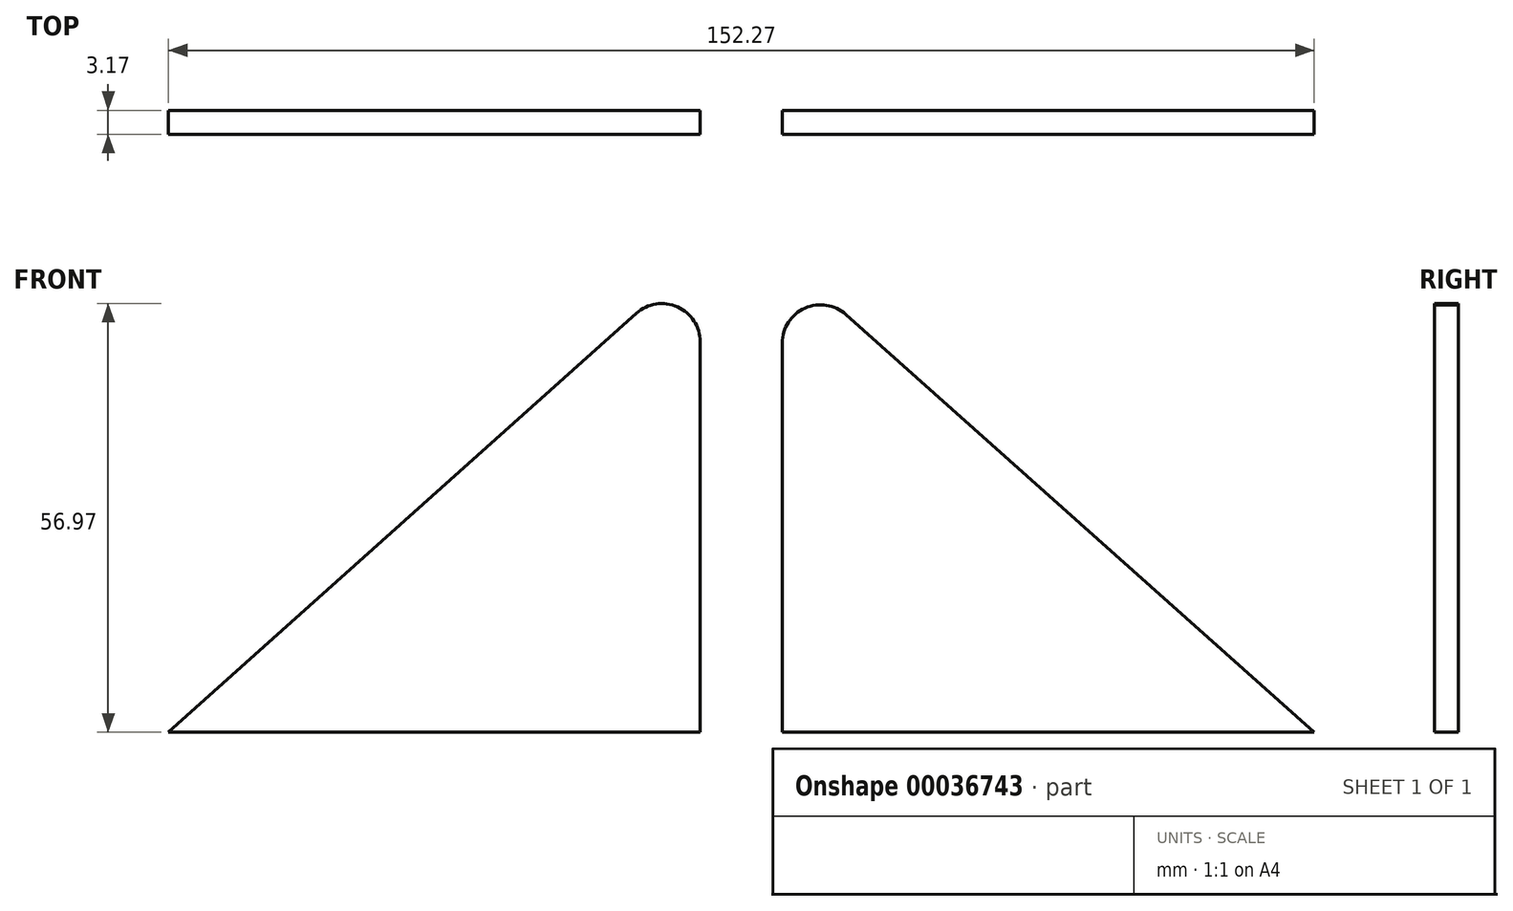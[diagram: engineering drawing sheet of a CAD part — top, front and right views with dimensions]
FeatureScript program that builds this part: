
annotation { "Feature Type Name" : "Feature", "Feature Type Description" : "" }
export const myFeature = defineFeature(function(context is Context, id is Id, definition is map)
    precondition{}
    {
        {
            var Q0;
            Q0=qCreatedBy(makeId("Front.planeOp"),FACE);
            var sketch = newSketch(context, id + "F0", { "sketchPlane" : qUnion([Q0])});
            skLineSegment(sketch, "E0", {"start": v(0, 63.5) * mm, "end": v(0, 0) * mm, "construction": true});
            skLineSegment(sketch, "E1", {"start": v(-5.58, 63.26) * mm, "end": v(-5.58, 0) * mm});
            skLineSegment(sketch, "E2", {"start": v(-5.58, 0) * mm, "end": v(-76.23, 0) * mm});
            skLineSegment(sketch, "E3", {"start": v(-76.23, 0) * mm, "end": v(-5.58, 63.26) * mm});
            skLineSegment(sketch, "E4", {"start": v(5.35, 63.06) * mm, "end": v(5.35, 0) * mm});
            skLineSegment(sketch, "E5", {"start": v(5.35, 0) * mm, "end": v(76.04, 0) * mm});
            skLineSegment(sketch, "E6", {"start": v(76.04, 0) * mm, "end": v(5.35, 63.06) * mm});
            skSolve(sketch);
        }
        {
            var Q0;
            Q0=makeQuery(id+"F0.imprint","IMPRINT",FACE,{"disambiguationData":[TD([[makeQuery(id+"F0.imprint","IMPRINT",EDGE,{"derivedFrom":sQuery(id+"F0.wireOp",EDGE,"E1")}),-1.0]])]});
            var Q1;
            Q1=makeQuery(id+"F0.imprint","IMPRINT",FACE,{"disambiguationData":[TD([[makeQuery(id+"F0.imprint","IMPRINT",EDGE,{"derivedFrom":sQuery(id+"F0.wireOp",EDGE,"E4")}),1.0]])]});
            extrude(context, id + "F1", {"entities" : qUnion([Q0, Q1]), "depth" : 3.17 * mm});
        }
        {
            var Q0;
            Q0=makeQuery(id+"F1.opExtrude","SWEPT_EDGE",EDGE,{"disambiguationData":[OSD([sQuery(id+"F0.wireOp",EDGE,"E4"),sQuery(id+"F0.wireOp",EDGE,"E6")])]});
            var Q1;
            Q1=makeQuery(id+"F1.opExtrude","SWEPT_EDGE",EDGE,{"disambiguationData":[OSD([sQuery(id+"F0.wireOp",EDGE,"E1"),sQuery(id+"F0.wireOp",EDGE,"E3")])]});
            fillet(context, id + "F2", {"entities" : qUnion([Q0, Q1]), "radius" : 5.08 * mm, "tangentPropagation" : true, "allowEdgeOverflow" : false});
        }
    });
